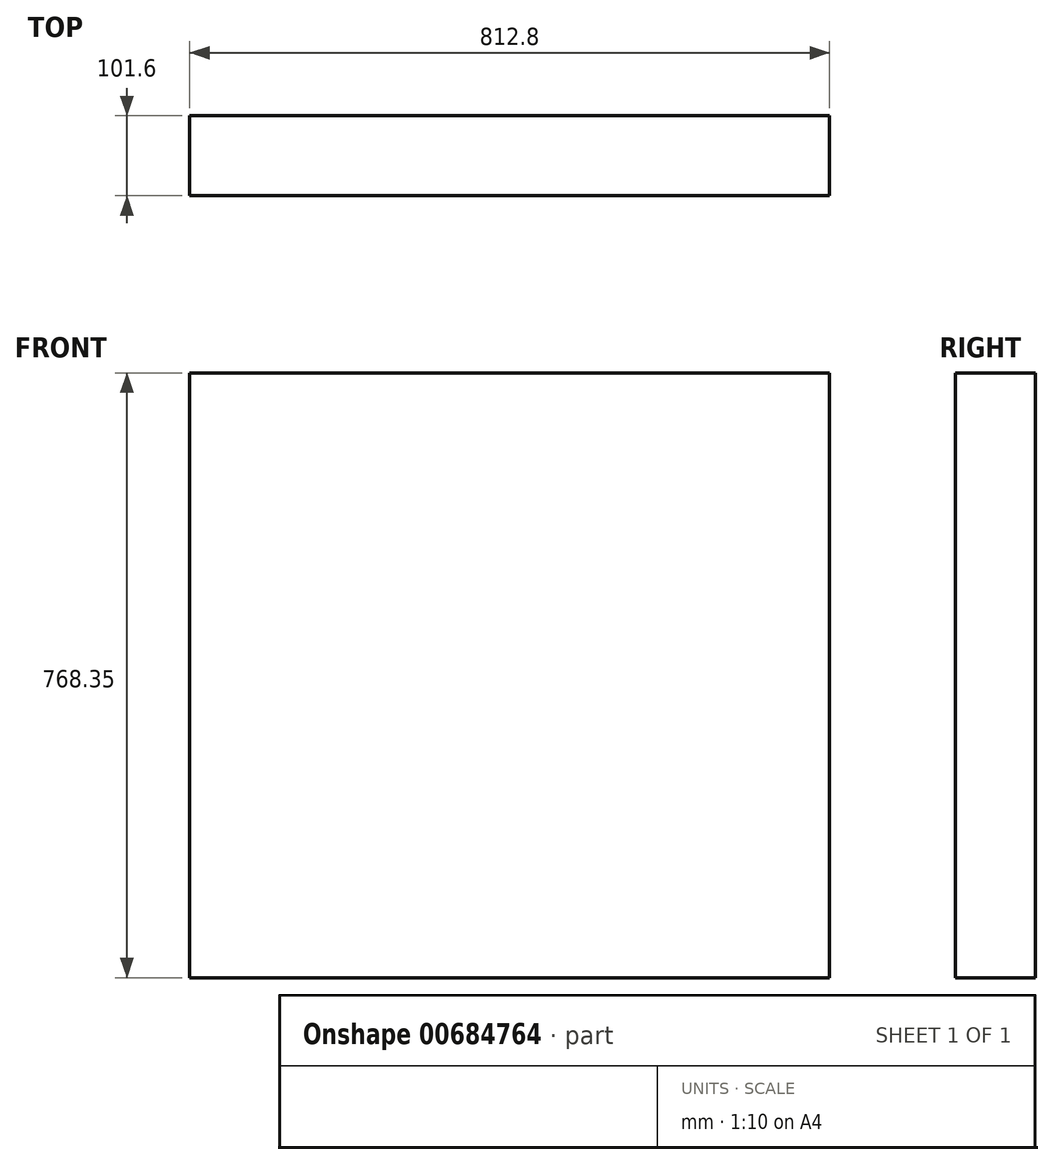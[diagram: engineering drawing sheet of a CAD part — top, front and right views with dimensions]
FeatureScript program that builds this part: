
annotation { "Feature Type Name" : "Feature", "Feature Type Description" : "" }
export const myFeature = defineFeature(function(context is Context, id is Id, definition is map)
    precondition{}
    {
        {
            var Q0;
            Q0=qCreatedBy(makeId("Right.planeOp"),FACE);
            var sketch = newSketch(context, id + "F0", { "sketchPlane" : qUnion([Q0])});
            skLineSegment(sketch, "E0.bottom", {"start": v(47.46, 667.55) * mm, "end": v(-54.14, 667.55) * mm});
            skLineSegment(sketch, "E0.top", {"start": v(47.46, -100.8) * mm, "end": v(-54.14, -100.8) * mm});
            skLineSegment(sketch, "E0.left", {"start": v(47.46, 667.55) * mm, "end": v(47.46, -100.8) * mm});
            skLineSegment(sketch, "E0.right", {"start": v(-54.14, 667.55) * mm, "end": v(-54.14, -100.8) * mm});
            skSolve(sketch);
        }
        {
            var Q0;
            Q0=qSketchRegion(id+"F0",true);
            extrude(context, id + "F1", {"entities" : qUnion([Q0]), "depth" : 812.8 * mm, "offsetDistance" : 25.4 * mm});
        }
    });
